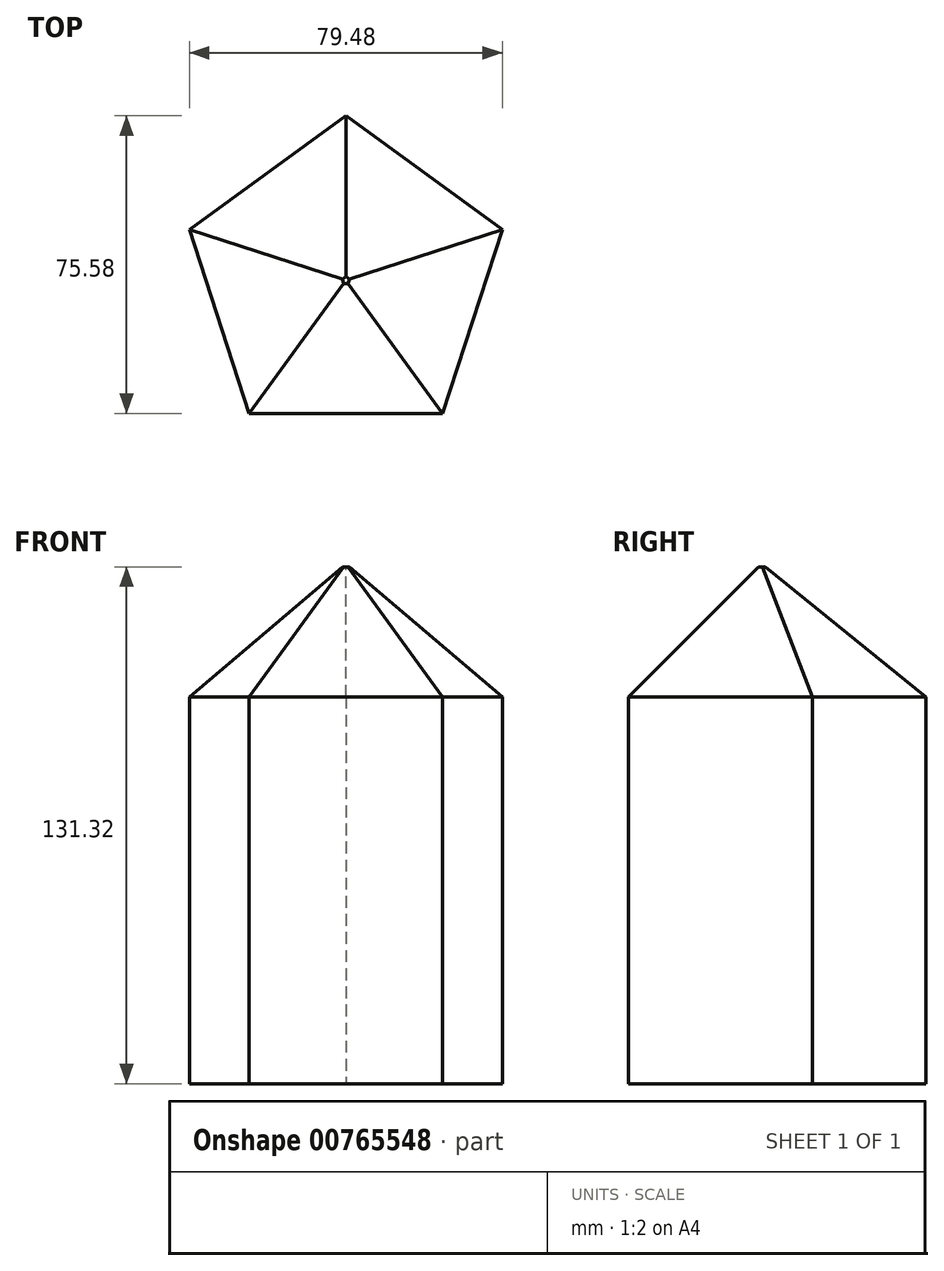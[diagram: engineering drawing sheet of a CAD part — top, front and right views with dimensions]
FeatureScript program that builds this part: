
annotation { "Feature Type Name" : "Feature", "Feature Type Description" : "" }
export const myFeature = defineFeature(function(context is Context, id is Id, definition is map)
    precondition{}
    {
        {
            var Q0;
            Q0=qCreatedBy(makeId("Top.planeOp"),FACE);
            var sketch = newSketch(context, id + "F0", { "sketchPlane" : qUnion([Q0])});
            skCircle(sketch, "E0.cCircle", {"center": v(0, 0) * mm, "radius": 33.8 * mm, "construction": true});
            skLineSegment(sketch, "E0.0", {"start": v(24.56, -33.8) * mm, "end": v(-24.56, -33.8) * mm});
            skLineSegment(sketch, "E0.1", {"start": v(-24.56, -33.8) * mm, "end": v(-39.74, 12.91) * mm});
            skLineSegment(sketch, "E0.2", {"start": v(-39.74, 12.91) * mm, "end": v(0, 41.78) * mm});
            skLineSegment(sketch, "E0.3", {"start": v(0, 41.78) * mm, "end": v(39.74, 12.91) * mm});
            skLineSegment(sketch, "E0.4", {"start": v(39.74, 12.91) * mm, "end": v(24.56, -33.8) * mm});
            skPoint(sketch, "E0.0.midPoint", {"position": v(0, -33.8) * mm});
            skSolve(sketch);
        }
        {
            var Q0;
            Q0=makeQuery(id+"F0.imprint","IMPRINT",FACE,{"disambiguationData":[TD([[makeQuery(id+"F0.imprint","IMPRINT",EDGE,{"derivedFrom":sQuery(id+"F0.wireOp",EDGE,"E0.0")}),-1.0]])]});
            extrude(context, id + "F1", {"entities" : qUnion([Q0]), "depth" : 131.32 * mm, "offsetDistance" : 25.4 * mm});
        }
        {
            var Q0;
            Q0=makeQuery(id+"F1.opExtrude","CAP_EDGE",EDGE,{"disambiguationData":[OSD([sQuery(id+"F0.wireOp",EDGE,"E0.0")])],"isStart":false});
            var Q1;
            Q1=makeQuery(id+"F1.opExtrude","CAP_EDGE",EDGE,{"disambiguationData":[OSD([sQuery(id+"F0.wireOp",EDGE,"E0.1")])],"isStart":false});
            var Q2;
            Q2=makeQuery(id+"F1.opExtrude","CAP_EDGE",EDGE,{"disambiguationData":[OSD([sQuery(id+"F0.wireOp",EDGE,"E0.2")])],"isStart":false});
            var Q3;
            Q3=makeQuery(id+"F1.opExtrude","CAP_EDGE",EDGE,{"disambiguationData":[OSD([sQuery(id+"F0.wireOp",EDGE,"E0.3")])],"isStart":false});
            var Q4;
            Q4=makeQuery(id+"F1.opExtrude","CAP_EDGE",EDGE,{"disambiguationData":[OSD([sQuery(id+"F0.wireOp",EDGE,"E0.4")])],"isStart":false});
            chamfer(context, id + "F2", {"entities" : qUnion([Q0, Q1, Q2, Q3, Q4]), "width" : 33.02 * mm, "tangentPropagation" : true});
        }
    });
